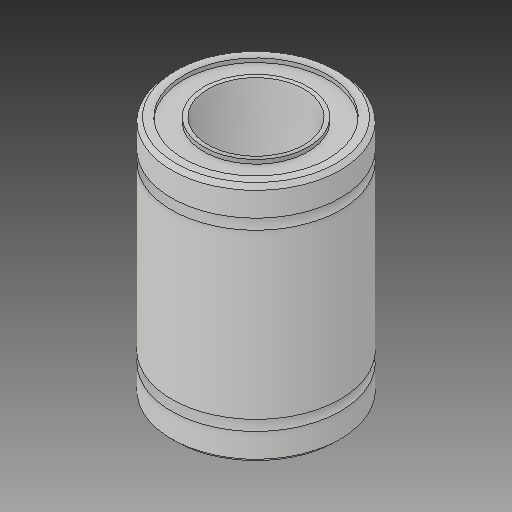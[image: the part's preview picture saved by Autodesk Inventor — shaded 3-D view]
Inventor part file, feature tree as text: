
AUTODESK INVENTOR PART (.ipt)
format: ipt  version: 2018 (Build 220112000, 112)  size: 166,400 bytes
history: native  units: mm
features: mirror x1
ambient origin geometry x8: Origin, YZ Plane, XZ Plane, XY Plane, X Axis, Y Axis, Z Axis, Center Point
bodies: Solid1 (feature_tree)
feature tree (1):
  mirror  "Mirror1"
